# Revit family: Low Pressure Rotary Screw Air Compressor
name_source: partatom
category: Mechanical Equipment
revit_build: Autodesk Revit 2015 (Build: 20150303_1515(x64)
units: mm (PartAtom-declared; Revit-internal decimal feet)

## types (3) — shared parameters
Base Height = 6' - 8"
Condensate Diameter = 0' - 0 3/8"
Connection Offset from Side of Unit = 0' - 1"
Description = LPAC-2
Display Height = 1' - 7 19/32"
Display Length = 1' - 8 29/32"
Display Screen Offset = 0' - 2"
Duct Connection Recess Depth = 0' - 2"
Electrical Inlet Diameter_UNKNOWN = 0' - 6"
Height Offset to Bottom of Display = 4' - 0 1/2"
Hood Scoop Arch Radius = 0' - 10"
Manufacturer = Ingersoll Rand.
Model = No Dryer Option, RR55-75)
Type Comments = Air-Cooled Rotary Screw Low Pressure Air Compressor
URL = Basis of Design - Equipment
Water Inlet/Outlet Diameter = 0' - 1 1/2"
Water Inlet/Outlet Height Offset = 0' - 2 13/16"
Water Outlet Offset from Inlet = 0' - 3 11/16"

## per-type parameters (varying)
| type | Air Connection_Duct Offset from Side of Unit | Air Connection_Duct_ Length | Air Connection_Duct_ Width | Air Inlet_Package Compressor Height | Air Inlet_Package Compressor Height Offset | Air Inlet_Package Compressor Offset from Side of Unit | Air Inlet_Package Compressor Width | Base Length | Base Width | Condensate Height Offset | Condensate Offset from Side of Unit | Discharge Air Diameter | Discharge Air Height Offset | Discharge Air Offset from Side of Unit | Electrical Inlet Height Offset | Electrical Inlet Offset from Side of Unit | Front of Unit to Air Connection Side | Hood Scoop Height | Hood Scoop Offset End From Side of Unit | Hood Scoop On/Off | Hood Scoop Start Offset from Side of Unit | Left of Unit to Display Face | Offset to Side of Display from Front | Water Inlet Offset from Side of Unit |
| LPAC-2 | 0' - 3 5/16" | 1' - 2 5/16" | 3' - 4 13/16" | 2' - 1 13/32" | 0' - 8 3/32" | 0' - 10 19/32" | 1' - 8 13/32" | 7' - 11 13/16" | 3' - 11 5/16" | 0' - 2 13/32" | 0' - 5 13/16" | 0' - 2" | 2' - 7 3/32" | 0' - 4 11/16" | 2' - 10 13/32" | 3' - 6 1/2" | 3' - 8 3/32" | 1' - 3 3/16" | 6' - 10 1/2" | Yes | 3' - 7 3/32" | 4' - 1 13/16" | 0' - 8 19/32" | 1' - 3 3/16" |
| LPAC-3 | 0' - 5" | 1' - 4 11/16" | 4' - 3 13/32" | 5' - 4 13/32" | 0' - 7" | 1' - 1 3/16" | 3' - 3" | 9' - 4 13/32" | 5' - 9 13/16" | 0' - 2" | 0' - 6 3/16" | 0' - 3" | 2' - 3 19/32" | 0' - 5 29/32" | 1' - 4 5/16" | 5' - 1 1/2" | 2' - 10 5/16" | 1' - 5 1/2" | 6' - 6 13/32" | No | 2' - 9 13/32" | 6' - 0 5/16" | 0' - 8 11/16" | 1' - 6 11/16" |
| LPAC-1 | 0' - 3 5/16" | 1' - 2 5/16" | 3' - 4 13/16" | 2' - 1 13/32" | 0' - 8 3/32" | 0' - 10 19/32" | 1' - 8 13/32" | 7' - 11 13/16" | 3' - 11 5/16" | 0' - 2 13/32" | 0' - 5 13/16" | 0' - 2" | 2' - 7 3/32" | 0' - 4 11/16" | 2' - 10 13/32" | 3' - 6 1/2" | 3' - 8 3/32" | 1' - 3 3/16" | 6' - 10 1/2" | Yes | 3' - 7 3/32" | 4' - 1 13/16" | 0' - 8 19/32" | 1' - 3 3/16" |

## geometry (parser evidence)
native form markers: Blend x2, Sweep x3
no freeform markers — native parametric forms only
